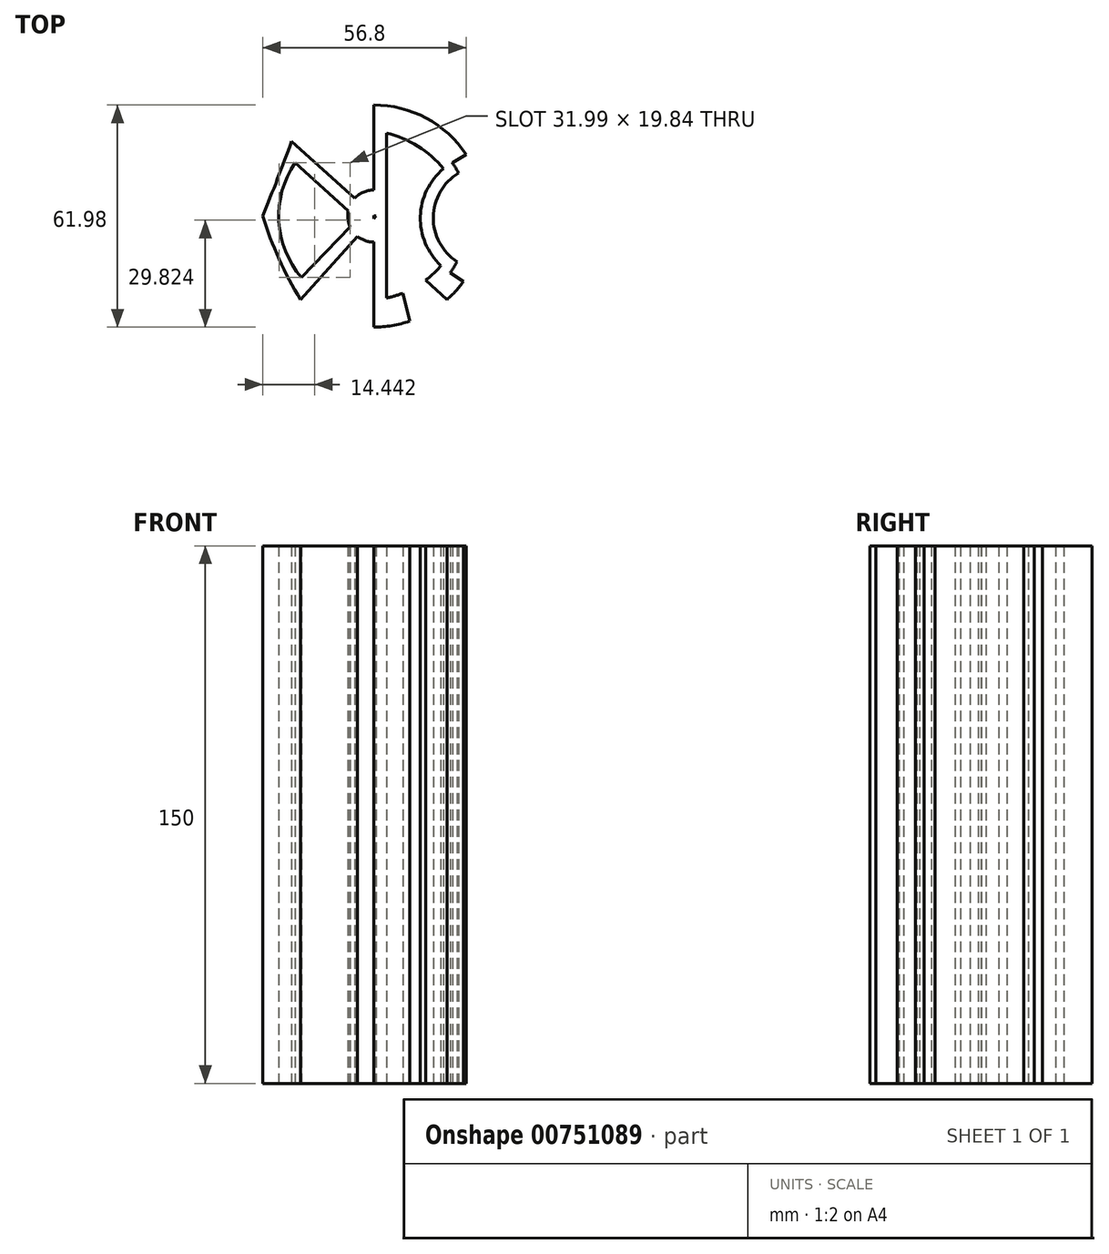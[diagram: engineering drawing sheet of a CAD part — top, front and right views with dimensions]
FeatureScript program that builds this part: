
annotation { "Feature Type Name" : "Feature", "Feature Type Description" : "" }
export const myFeature = defineFeature(function(context is Context, id is Id, definition is map)
    precondition{}
    {
        {
            var Q0;
            Q0=qCreatedBy(makeId("Top.planeOp"),FACE);
            var sketch = newSketch(context, id + "F0", { "sketchPlane" : qUnion([Q0])});
            skArc(sketch, "E0", {"start": v(-21.97, 14.83) * mm, "mid": v(-26.47, -1.46) * mm, "end": v(-20.2, -17.16) * mm});
            skLineSegment(sketch, "E1", {"start": v(0, 31) * mm, "end": v(0, 7.26) * mm});
            skLineSegment(sketch, "E2", {"start": v(-22.93, 20.85) * mm, "end": v(-5.3, 4.97) * mm});
            skArc(sketch, "E3", {"start": v(0, 7.26) * mm, "mid": v(-2.89, 6.67) * mm, "end": v(-5.3, 4.97) * mm});
            skArc(sketch, "E4.trimOffspring", {"start": v(21.3, -15.79) * mm, "mid": v(22.32, -14.3) * mm, "end": v(23.24, -12.76) * mm});
            skArc(sketch, "E5.trimOffspring", {"start": v(0, -31) * mm, "mid": v(5.1, -30.57) * mm, "end": v(10.06, -29.32) * mm});
            skLineSegment(sketch, "E6.trimOffspring", {"start": v(0.63, 0) * mm, "end": v(0, -0.7) * mm});
            skLineSegment(sketch, "E7.trimOffspring", {"start": v(0, 0) * mm, "end": v(0.63, 0) * mm});
            skPoint(sketch, "E8.start.orphan", {"position": v(-31, 0) * mm});
            skLineSegment(sketch, "E9.trimOffspring", {"start": v(0, 0.2) * mm, "end": v(0, -31) * mm});
            skLineSegment(sketch, "E10.trimOffspring", {"start": v(0, 0.2) * mm, "end": v(0.44, -0.2) * mm});
            skLineSegment(sketch, "E11.trimOffspring", {"start": v(-4.5, -5.7) * mm, "end": v(-20.4, -23.34) * mm});
            skArc(sketch, "E12", {"start": v(-31, 0) * mm, "mid": v(-26.85, 10.38) * mm, "end": v(-22.93, 20.85) * mm});
            skArc(sketch, "E13", {"start": v(-31, 0) * mm, "mid": v(-26.42, -12) * mm, "end": v(-20.4, -23.34) * mm});
            skLineSegment(sketch, "E14", {"start": v(-21.97, 14.83) * mm, "end": v(-7.12, 1.45) * mm});
            skLineSegment(sketch, "E15", {"start": v(-6.63, -2.98) * mm, "end": v(-20.2, -17.16) * mm});
            skArc(sketch, "E16.trimOffspring", {"start": v(-4.5, -5.7) * mm, "mid": v(-2.38, -6.86) * mm, "end": v(0, -7.26) * mm});
            skArc(sketch, "E17.trimOffspring", {"start": v(-7.12, 1.45) * mm, "mid": v(-7.22, -0.8) * mm, "end": v(-6.63, -2.98) * mm});
            skArc(sketch, "E18", {"start": v(19.47, 13.18) * mm, "mid": v(13, -0.15) * mm, "end": v(18.74, -13.81) * mm});
            skArc(sketch, "E19", {"start": v(23.65, 11.97) * mm, "mid": v(16.6, -0.28) * mm, "end": v(23.24, -12.76) * mm});
            skLineSegment(sketch, "E20", {"start": v(21.3, -15.79) * mm, "end": v(25.08, -18.2) * mm});
            skLineSegment(sketch, "E21", {"start": v(21.93, 14.9) * mm, "end": v(25.81, 17.15) * mm});
            skArc(sketch, "E22.trimOffspring", {"start": v(23.65, 11.97) * mm, "mid": v(22.84, 13.46) * mm, "end": v(21.93, 14.9) * mm});
            skArc(sketch, "E23.trimOffspring", {"start": v(25.81, 17.15) * mm, "mid": v(14.65, 27.32) * mm, "end": v(0, 31) * mm});
            skArc(sketch, "E24", {"start": v(3.56, -22.87) * mm, "mid": v(5.85, -22.3) * mm, "end": v(8.1, -21.53) * mm});
            skLineSegment(sketch, "E25", {"start": v(3.56, 23.12) * mm, "end": v(3.56, -22.87) * mm});
            skArc(sketch, "E26", {"start": v(19.47, 13.18) * mm, "mid": v(12.34, 19.47) * mm, "end": v(3.56, 23.12) * mm});
            skLineSegment(sketch, "E27", {"start": v(8.1, -21.53) * mm, "end": v(10.06, -29.32) * mm});
            skLineSegment(sketch, "E28", {"start": v(14.46, -17.92) * mm, "end": v(20.44, -23.3) * mm});
            skArc(sketch, "E29.trimOffspring", {"start": v(14.46, -17.92) * mm, "mid": v(16.71, -15.98) * mm, "end": v(18.74, -13.81) * mm});
            skArc(sketch, "E30.trimOffspring", {"start": v(20.44, -23.3) * mm, "mid": v(22.9, -20.88) * mm, "end": v(25.08, -18.2) * mm});
            skSolve(sketch);
        }
        {
            var Q0;
            Q0=makeQuery(id+"F0.imprint","IMPRINT",FACE,{"disambiguationData":[TD([[makeQuery(id+"F0.imprint","IMPRINT",EDGE,{"derivedFrom":sQuery(id+"F0.wireOp",EDGE,"E0")}),-1.0]])]});
            extrude(context, id + "F1", {"entities" : qUnion([Q0]), "depth" : 150 * mm, "offsetDistance" : 25 * mm});
        }
    });
